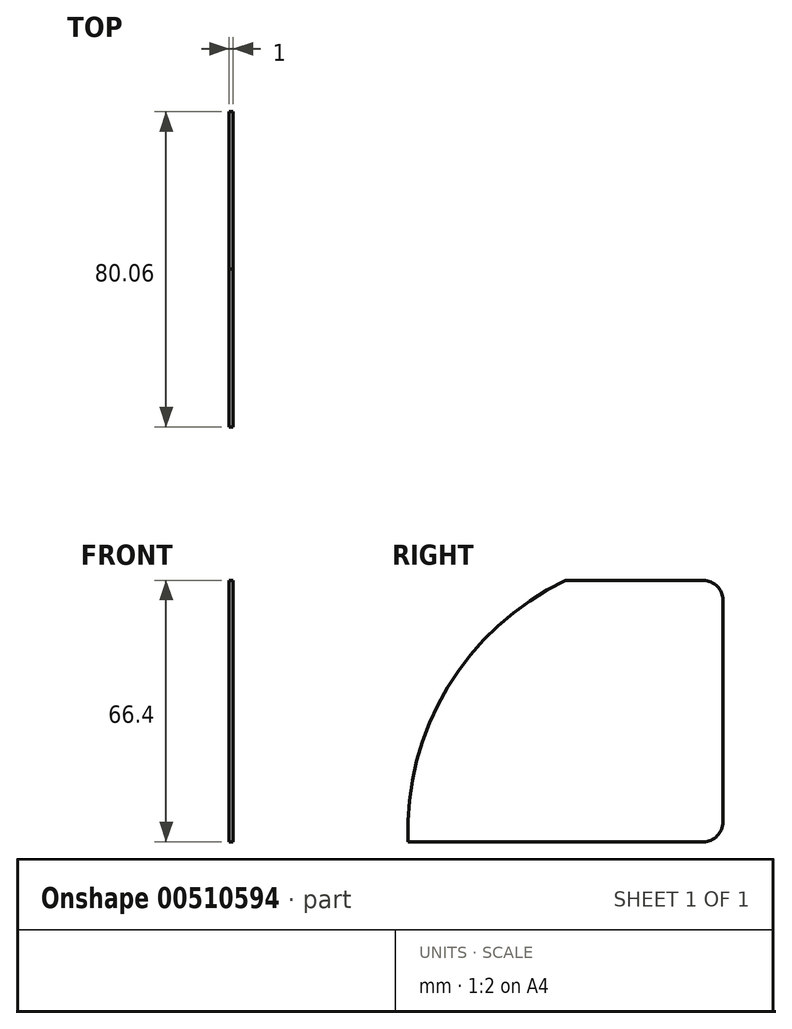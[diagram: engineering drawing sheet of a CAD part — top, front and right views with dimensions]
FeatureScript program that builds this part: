
annotation { "Feature Type Name" : "Feature", "Feature Type Description" : "" }
export const myFeature = defineFeature(function(context is Context, id is Id, definition is map)
    precondition{}
    {
        {
            var Q0;
            Q0=qCreatedBy(makeId("Right.planeOp"),FACE);
            var sketch = newSketch(context, id + "F0", { "sketchPlane" : qUnion([Q0])});
            skLineSegment(sketch, "E0", {"start": v(-5, 0) * mm, "end": v(-80, 0) * mm});
            skLineSegment(sketch, "E1", {"start": v(0, 5) * mm, "end": v(0, 61.4) * mm});
            skLineSegment(sketch, "E2", {"start": v(-5, 66.4) * mm, "end": v(-40, 66.4) * mm});
            skArc(sketch, "E3", {"start": v(-40, 66.4) * mm, "mid": v(-69.98, 39.21) * mm, "end": v(-80, 0) * mm});
            skPoint(sketch, "E4.visualSharp", {"position": v(0, 66.4) * mm});
            skArc(sketch, "E4.filletArc", {"start": v(0, 61.4) * mm, "mid": v(-1.46, 64.94) * mm, "end": v(-5, 66.4) * mm});
            skPoint(sketch, "E5.visualSharp", {"position": v(0, 0) * mm});
            skArc(sketch, "E5.filletArc", {"start": v(-5, 0) * mm, "mid": v(-1.46, 1.46) * mm, "end": v(0, 5) * mm});
            skSolve(sketch);
        }
        {
            var Q0;
            Q0=makeQuery(id+"F0.imprint","IMPRINT",FACE,{"disambiguationData":[TD([[makeQuery(id+"F0.imprint","IMPRINT",EDGE,{"derivedFrom":sQuery(id+"F0.wireOp",EDGE,"E0")}),-1.0]])]});
            extrude(context, id + "F1", {"entities" : qUnion([Q0]), "depth" : 1 * mm});
        }
    });
